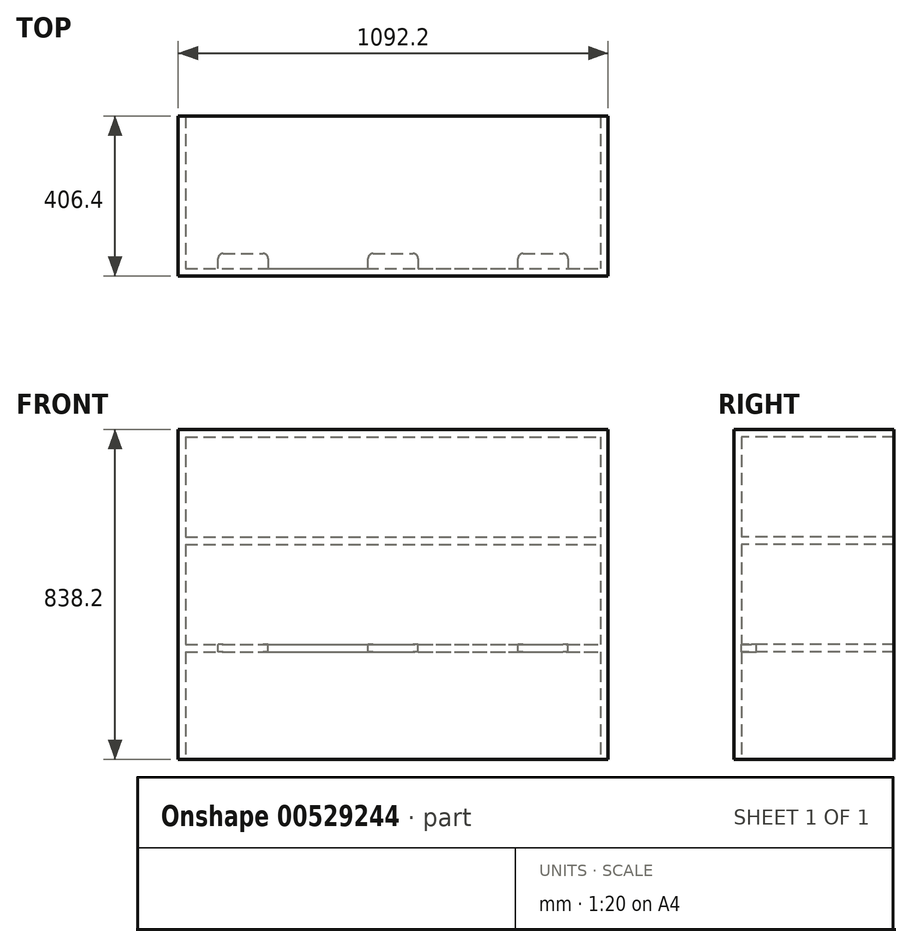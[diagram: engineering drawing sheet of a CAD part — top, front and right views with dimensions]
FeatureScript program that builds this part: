
annotation { "Feature Type Name" : "Feature", "Feature Type Description" : "" }
export const myFeature = defineFeature(function(context is Context, id is Id, definition is map)
    precondition{}
    {
        {
            var Q0;
            Q0=qCreatedBy(makeId("Front.planeOp"),FACE);
            var sketch = newSketch(context, id + "F0", { "sketchPlane" : qUnion([Q0])});
            skLineSegment(sketch, "E0.bottom", {"start": v(-537.31, 838.2) * mm, "end": v(554.89, 838.2) * mm});
            skLineSegment(sketch, "E0.top", {"start": v(-537.31, 0) * mm, "end": v(554.89, 0) * mm});
            skLineSegment(sketch, "E0.left", {"start": v(-537.31, 838.2) * mm, "end": v(-537.31, 0) * mm});
            skLineSegment(sketch, "E0.right", {"start": v(554.89, 838.2) * mm, "end": v(554.89, 0) * mm});
            skSolve(sketch);
        }
        {
            var Q0;
            Q0 = qSketchRegion(id + "F0", true);
            extrude(context, id + "F1", {"entities" : qUnion([Q0]), "depth" : 19.05 * mm, "offsetDistance" : 25.4 * mm});
        }
        {
            var Q0;
            Q0=makeQuery(id+"F1.opExtrude","CAP_FACE",FACE,{"disambiguationData":[OSD([sQuery(id+"F0.wireOp",EDGE,"E0.bottom"),sQuery(id+"F0.wireOp",EDGE,"E0.top"),sQuery(id+"F0.wireOp",EDGE,"E0.left"),sQuery(id+"F0.wireOp",EDGE,"E0.right")])],"isStart":true});
            var sketch = newSketch(context, id + "F2", { "sketchPlane" : qUnion([Q0])});
            skLineSegment(sketch, "E1.bottom", {"start": v(537.31, 838.2) * mm, "end": v(518.26, 838.2) * mm});
            skLineSegment(sketch, "E1.top", {"start": v(537.31, 0) * mm, "end": v(518.26, 0) * mm});
            skLineSegment(sketch, "E1.left", {"start": v(537.31, 838.2) * mm, "end": v(537.31, 0) * mm});
            skLineSegment(sketch, "E1.right", {"start": v(518.26, 819.15) * mm, "end": v(518.26, 565.15) * mm});
            skLineSegment(sketch, "E2.bottom", {"start": v(518.26, 838.2) * mm, "end": v(-535.84, 838.2) * mm});
            skLineSegment(sketch, "E2.top", {"start": v(518.26, 819.15) * mm, "end": v(-535.84, 819.15) * mm});
            skLineSegment(sketch, "E3.bottom", {"start": v(-535.84, 838.2) * mm, "end": v(-554.89, 838.2) * mm});
            skLineSegment(sketch, "E3.top", {"start": v(-535.84, 0) * mm, "end": v(-554.89, 0) * mm});
            skLineSegment(sketch, "E3.left", {"start": v(-535.84, 819.15) * mm, "end": v(-535.84, 565.15) * mm});
            skLineSegment(sketch, "E3.right", {"start": v(-554.89, 838.2) * mm, "end": v(-554.89, 0) * mm});
            skLineSegment(sketch, "E4.bottom", {"start": v(518.26, 565.15) * mm, "end": v(-535.84, 565.15) * mm});
            skLineSegment(sketch, "E4.top", {"start": v(518.26, 546.1) * mm, "end": v(-535.84, 546.1) * mm});
            skLineSegment(sketch, "E5.bottom", {"start": v(518.26, 292.1) * mm, "end": v(-535.84, 292.1) * mm});
            skLineSegment(sketch, "E5.top", {"start": v(518.26, 273.05) * mm, "end": v(-535.84, 273.05) * mm});
            skLineSegment(sketch, "E6.trimOffspring", {"start": v(-535.84, 546.1) * mm, "end": v(-535.84, 292.1) * mm});
            skLineSegment(sketch, "E7.trimOffspring", {"start": v(518.26, 546.1) * mm, "end": v(518.26, 292.1) * mm});
            skLineSegment(sketch, "E8.trimOffspring", {"start": v(518.26, 273.05) * mm, "end": v(518.26, 0) * mm});
            skLineSegment(sketch, "E9.trimOffspring", {"start": v(-535.84, 273.05) * mm, "end": v(-535.84, 0) * mm});
            skSolve(sketch);
        }
        {
            var Q0;
            Q0 = qSketchRegion(id + "F2", true);
            extrude(context, id + "F3", {"entities" : qUnion([Q0]), "operationType" : NewBodyOperationType.ADD, "depth" : 387.35 * mm, "offsetDistance" : 25.4 * mm});
        }
        {
            var Q0;
            Q0=makeQuery(id+"F3.opExtrude","SWEPT_FACE",FACE,{"disambiguationData":[OSD([sQuery(id+"F2.wireOp",EDGE,"E5.bottom")])]});
            var sketch = newSketch(context, id + "F4", { "sketchPlane" : qUnion([Q0])});
            skLineSegment(sketch, "E10", {"start": v(-435.71, 0) * mm, "end": v(-435.71, 25.4) * mm});
            skLineSegment(sketch, "E11", {"start": v(-423.01, 38.1) * mm, "end": v(-321.41, 38.1) * mm});
            skLineSegment(sketch, "E12", {"start": v(-308.71, 25.4) * mm, "end": v(-308.71, 0) * mm});
            skPoint(sketch, "E13.visualSharp", {"position": v(-435.71, 38.1) * mm});
            skArc(sketch, "E13.filletArc", {"start": v(-423.01, 38.1) * mm, "mid": v(-432, 34.38) * mm, "end": v(-435.71, 25.4) * mm});
            skPoint(sketch, "E14.visualSharp", {"position": v(-308.71, 38.1) * mm});
            skArc(sketch, "E14.filletArc", {"start": v(-308.71, 25.4) * mm, "mid": v(-312.43, 34.38) * mm, "end": v(-321.41, 38.1) * mm});
            skLineSegment(sketch, "E15.1.0.0", {"start": v(-54.71, 0) * mm, "end": v(-54.71, 25.4) * mm});
            skLineSegment(sketch, "E15.1.0.1", {"start": v(-42.01, 38.1) * mm, "end": v(59.59, 38.1) * mm});
            skArc(sketch, "E15.1.0.2", {"start": v(-42.01, 38.1) * mm, "mid": v(-51, 34.38) * mm, "end": v(-54.71, 25.4) * mm});
            skArc(sketch, "E15.1.0.3", {"start": v(72.29, 25.4) * mm, "mid": v(68.57, 34.38) * mm, "end": v(59.59, 38.1) * mm});
            skLineSegment(sketch, "E15.1.0.4", {"start": v(72.29, 25.4) * mm, "end": v(72.29, 0) * mm});
            skLineSegment(sketch, "E15.2.0.0", {"start": v(326.29, 0) * mm, "end": v(326.29, 25.4) * mm});
            skLineSegment(sketch, "E15.2.0.1", {"start": v(338.99, 38.1) * mm, "end": v(440.59, 38.1) * mm});
            skArc(sketch, "E15.2.0.2", {"start": v(338.99, 38.1) * mm, "mid": v(330, 34.38) * mm, "end": v(326.29, 25.4) * mm});
            skArc(sketch, "E15.2.0.3", {"start": v(453.29, 25.4) * mm, "mid": v(449.57, 34.38) * mm, "end": v(440.59, 38.1) * mm});
            skLineSegment(sketch, "E15.2.0.4", {"start": v(453.29, 25.4) * mm, "end": v(453.29, 0) * mm});
            skLineSegment(sketch, "E15.direction1", {"start": v(-435.71, 0) * mm, "end": v(-54.71, 0) * mm, "construction": true});
            skLineSegment(sketch, "E16", {"start": v(-435.71, 0) * mm, "end": v(-308.71, 0) * mm});
            skLineSegment(sketch, "E17", {"start": v(-54.71, 0) * mm, "end": v(72.29, 0) * mm});
            skLineSegment(sketch, "E18", {"start": v(326.29, 0) * mm, "end": v(453.29, 0) * mm});
            skSolve(sketch);
        }
        {
            var Q0;
            Q0 = qSketchRegion(id + "F4", true);
            extrude(context, id + "F5", {"entities" : qUnion([Q0]), "operationType" : NewBodyOperationType.REMOVE, "oppositeDirection" : true, "depth" : 19.05 * mm, "offsetDistance" : 25.4 * mm});
        }
    });
